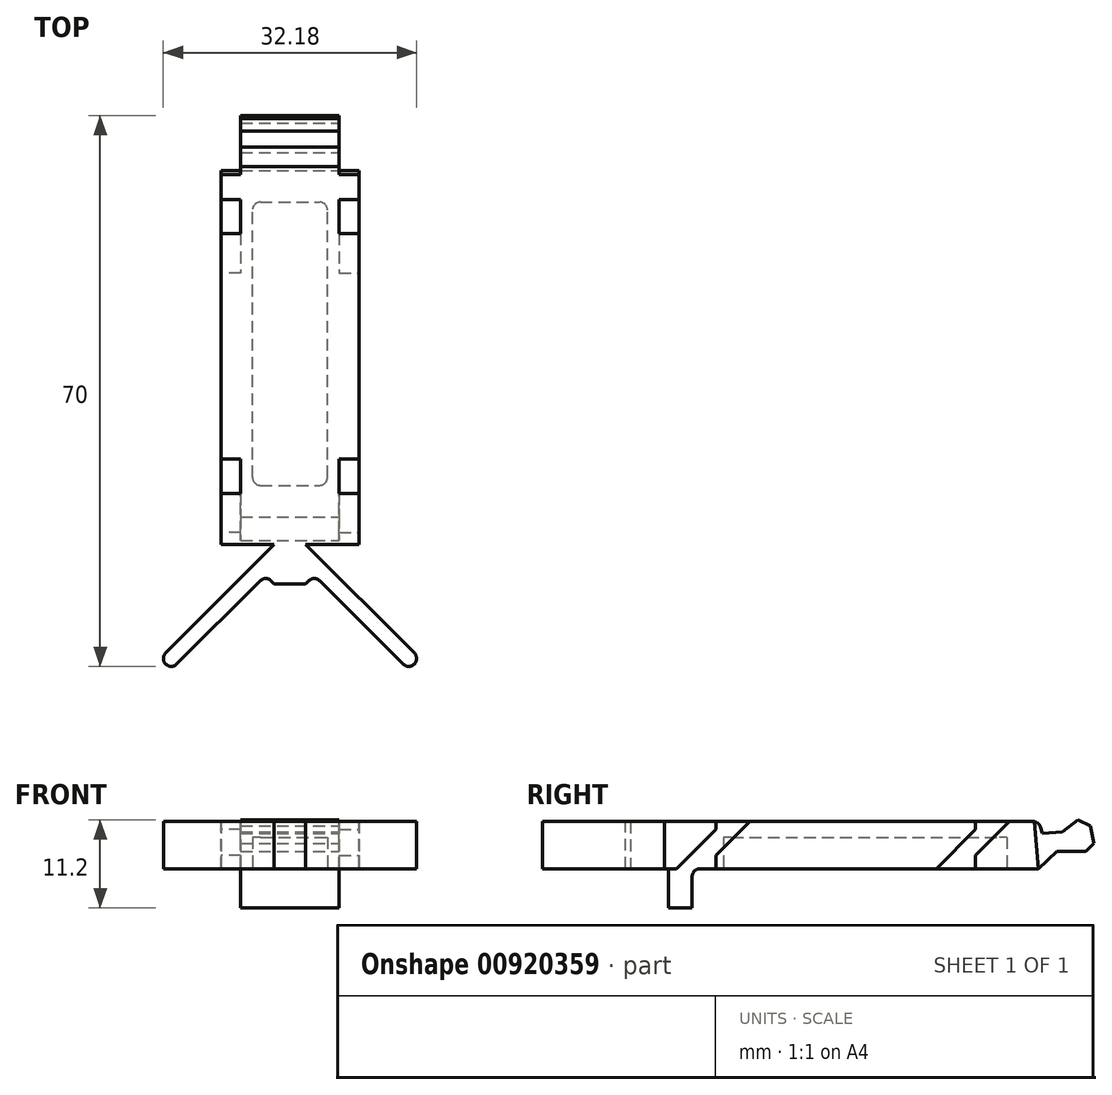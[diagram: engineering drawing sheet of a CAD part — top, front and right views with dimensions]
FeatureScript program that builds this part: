
annotation { "Feature Type Name" : "Feature", "Feature Type Description" : "" }
export const myFeature = defineFeature(function(context is Context, id is Id, definition is map)
    precondition{}
    {
        {
            var Q0;
            Q0=qCreatedBy(makeId("Right.planeOp"),FACE);
            var sketch = newSketch(context, id + "F0", { "sketchPlane" : qUnion([Q0])});
            skLineSegment(sketch, "E0.bottom", {"start": v(3, 0) * mm, "end": v(47, 0) * mm});
            skLineSegment(sketch, "E0.top", {"start": v(-0.5, 6) * mm, "end": v(47, 6) * mm});
            skLineSegment(sketch, "E1", {"start": v(47, 6) * mm, "end": v(47.5, 4.5) * mm});
            skLineSegment(sketch, "E2", {"start": v(47.5, 4.5) * mm, "end": v(50, 4.7) * mm});
            skLineSegment(sketch, "E3", {"start": v(52, 6.2) * mm, "end": v(50, 4.7) * mm});
            skLineSegment(sketch, "E4", {"start": v(52, 6.2) * mm, "end": v(53.6, 5.45) * mm});
            skLineSegment(sketch, "E5", {"start": v(53.6, 5.45) * mm, "end": v(54, 3.2) * mm});
            skLineSegment(sketch, "E6", {"start": v(53, 2.2) * mm, "end": v(54, 3.2) * mm});
            skLineSegment(sketch, "E7", {"start": v(53, 2.2) * mm, "end": v(49.3, 2.2) * mm});
            skLineSegment(sketch, "E8", {"start": v(49.3, 2.2) * mm, "end": v(47, 0) * mm});
            skLineSegment(sketch, "E9.top", {"start": v(0, -5) * mm, "end": v(3, -5) * mm});
            skLineSegment(sketch, "E9.left", {"start": v(0, 0) * mm, "end": v(0, -5) * mm});
            skLineSegment(sketch, "E9.right", {"start": v(3, 0) * mm, "end": v(3, -5) * mm});
            skLineSegment(sketch, "E10", {"start": v(0, 0) * mm, "end": v(-0.5, 0) * mm});
            skLineSegment(sketch, "E11", {"start": v(-0.5, 0) * mm, "end": v(-0.5, 6) * mm});
            skSolve(sketch);
        }
        {
            var Q0;
            Q0=makeQuery(id+"F0.imprint","IMPRINT",FACE,{"disambiguationData":[TD([[makeQuery(id+"F0.imprint","IMPRINT",EDGE,{"derivedFrom":sQuery(id+"F0.wireOp",EDGE,"E0.bottom")}),1.0]])]});
            extrude(context, id + "F1", {"entities" : qUnion([Q0]), "oppositeDirection" : true, "depth" : (17.5 / 2) * mm, "offsetDistance" : 25 * mm});
        }
        {
            var Q0;
            Q0=makeQuery(id+"F1.opExtrude","CAP_FACE",FACE,{"disambiguationData":[OSD([sQuery(id+"F0.wireOp",EDGE,"E0.bottom"),sQuery(id+"F0.wireOp",EDGE,"E0.top"),sQuery(id+"F0.wireOp",EDGE,"E0.left"),sQuery(id+"F0.wireOp",EDGE,"E1"),sQuery(id+"F0.wireOp",EDGE,"E2"),sQuery(id+"F0.wireOp",EDGE,"E3"),sQuery(id+"F0.wireOp",EDGE,"E4"),sQuery(id+"F0.wireOp",EDGE,"E5"),sQuery(id+"F0.wireOp",EDGE,"E6"),sQuery(id+"F0.wireOp",EDGE,"E7"),sQuery(id+"F0.wireOp",EDGE,"E8"),sQuery(id+"F0.wireOp",EDGE,"aNBXXahW-gOjJ-Jwd1-zqlN-Yp4owCK9dqC5"),sQuery(id+"F0.wireOp",EDGE,"ZARCzN4I-FOhr-0KRS-TbkK-G5KhNvsp9BvJ"),sQuery(id+"F0.wireOp",EDGE,"wQh7WQI4-VwIE-I1oY-PVTZ-LHgqh0pQGRtQ"),sQuery(id+"F0.wireOp",EDGE,"8AAlagfr-6v5t-paXQ-9fkX-cdchTd0ztlK5"),sQuery(id+"F0.wireOp",EDGE,"tXMYSlsr-eLFK-F21U-8xQ6-JhVVK3gynAGm")])],"isStart":true});
            var sketch = newSketch(context, id + "F2", { "sketchPlane" : qUnion([Q0])});
            skLineSegment(sketch, "E12", {"start": v(10.32, 6) * mm, "end": v(6, 1.68) * mm});
            skLineSegment(sketch, "E13", {"start": v(6, 0) * mm, "end": v(8, 0) * mm});
            skLineSegment(sketch, "E14", {"start": v(8, 0) * mm, "end": v(8, -7.24) * mm});
            skLineSegment(sketch, "E15", {"start": v(8, -7.24) * mm, "end": v(-4.58, -7.24) * mm});
            skLineSegment(sketch, "E16", {"start": v(-4.58, -7.24) * mm, "end": v(-4.58, 0) * mm});
            skLineSegment(sketch, "E17", {"start": v(-4.58, 0) * mm, "end": v(1, 0) * mm});
            skLineSegment(sketch, "E18", {"start": v(1, 0) * mm, "end": v(6, 5) * mm});
            skLineSegment(sketch, "E19", {"start": v(6, 5) * mm, "end": v(6, 6) * mm});
            skLineSegment(sketch, "E20", {"start": v(6, 6) * mm, "end": v(10.32, 6) * mm});
            skLineSegment(sketch, "E21", {"start": v(6, 1.68) * mm, "end": v(6, 0) * mm});
            skLineSegment(sketch, "E22.1.0.0", {"start": v(39, 0) * mm, "end": v(41, 0) * mm});
            skLineSegment(sketch, "E22.1.0.1", {"start": v(39, 5) * mm, "end": v(39, 6) * mm});
            skLineSegment(sketch, "E22.1.0.2", {"start": v(41, -7.24) * mm, "end": v(28.42, -7.24) * mm});
            skLineSegment(sketch, "E22.1.0.3", {"start": v(39, 1.68) * mm, "end": v(39, 0) * mm});
            skLineSegment(sketch, "E22.1.0.4", {"start": v(41, 0) * mm, "end": v(41, -7.24) * mm});
            skLineSegment(sketch, "E22.1.0.5", {"start": v(39, 6) * mm, "end": v(43.32, 6) * mm});
            skLineSegment(sketch, "E22.1.0.6", {"start": v(28.42, 0) * mm, "end": v(34, 0) * mm});
            skLineSegment(sketch, "E22.1.0.7", {"start": v(28.42, -7.24) * mm, "end": v(28.42, 0) * mm});
            skLineSegment(sketch, "E22.1.0.8", {"start": v(34, 0) * mm, "end": v(39, 5) * mm});
            skLineSegment(sketch, "E22.1.0.9", {"start": v(43.32, 6) * mm, "end": v(39, 1.68) * mm});
            skLineSegment(sketch, "E22.2.0.0", {"start": v(72, 0) * mm, "end": v(74, 0) * mm});
            skLineSegment(sketch, "E22.2.0.1", {"start": v(72, 5) * mm, "end": v(72, 6) * mm});
            skLineSegment(sketch, "E22.2.0.2", {"start": v(74, -7.24) * mm, "end": v(61.42, -7.24) * mm});
            skLineSegment(sketch, "E22.2.0.3", {"start": v(72, 1.68) * mm, "end": v(72, 0) * mm});
            skLineSegment(sketch, "E22.2.0.4", {"start": v(74, 0) * mm, "end": v(74, -7.24) * mm});
            skLineSegment(sketch, "E22.2.0.5", {"start": v(72, 6) * mm, "end": v(76.32, 6) * mm});
            skLineSegment(sketch, "E22.2.0.6", {"start": v(61.42, 0) * mm, "end": v(67, 0) * mm});
            skLineSegment(sketch, "E22.2.0.7", {"start": v(61.42, -7.24) * mm, "end": v(61.42, 0) * mm});
            skLineSegment(sketch, "E22.2.0.8", {"start": v(67, 0) * mm, "end": v(72, 5) * mm});
            skLineSegment(sketch, "E22.2.0.9", {"start": v(76.32, 6) * mm, "end": v(72, 1.68) * mm});
            skLineSegment(sketch, "E22.direction1", {"start": v(-4.58, -7.24) * mm, "end": v(28.42, -7.24) * mm, "construction": true});
            skSolve(sketch);
        }
        {
            var Q0;
            Q0 = qSketchRegion(id + "F2", true);
            extrude(context, id + "F3", {"entities" : qUnion([Q0]), "operationType" : NewBodyOperationType.REMOVE, "oppositeDirection" : true, "depth" : 2.5 * mm, "offsetDistance" : 25 * mm});
        }
        {
            var Q0;
            Q0=makeQuery(id+"F1.opExtrude","SWEPT_EDGE",EDGE,{"disambiguationData":[OSD([sQuery(id+"F0.wireOp",EDGE,"E0.top"),sQuery(id+"F0.wireOp",EDGE,"E1")])]});
            fillet(context, id + "F4", {"entities" : qUnion([Q0]), "radius" : 1 * mm, "tangentPropagation" : true, "allowEdgeOverflow" : false});
        }
        {
            var Q0;
            Q0=makeQuery(id+"F1.opExtrude","SWEPT_FACE",FACE,{"disambiguationData":[OSD([sQuery(id+"F0.wireOp",EDGE,"E0.top")])]});
            var sketch = newSketch(context, id + "F5", { "sketchPlane" : qUnion([Q0])});
            skLineSegment(sketch, "E23", {"start": v(-8.75, -0.5) * mm, "end": v(-8.75, -5.5) * mm});
            skLineSegment(sketch, "E24", {"start": v(-8.75, -5.5) * mm, "end": v(-6.75, -5.5) * mm});
            skLineSegment(sketch, "E25", {"start": v(-6.75, -5.5) * mm, "end": v(-5.66, -4.41) * mm});
            skLineSegment(sketch, "E26", {"start": v(-5.66, -4.41) * mm, "end": v(5.63, -15.7) * mm});
            skLineSegment(sketch, "E27", {"start": v(7.04, -14.3) * mm, "end": v(-6.75, -0.5) * mm});
            skLineSegment(sketch, "E28", {"start": v(-6.75, -0.5) * mm, "end": v(-8.75, -0.5) * mm});
            skArc(sketch, "E29", {"start": v(5.63, -15.7) * mm, "mid": v(7.04, -15.7) * mm, "end": v(7.04, -14.3) * mm});
            skSolve(sketch);
        }
        {
            var Q0;
            Q0 = qSketchRegion(id + "F5", true);
            var Q1;
            Q1=makeQuery(id+"F3.boolean.opBoolean","MERGE",FACE,{"derivedFrom":[makeQuery(id+"F1.opExtrude","SWEPT_FACE",FACE,{"disambiguationData":[OSD([sQuery(id+"F0.wireOp",EDGE,"E10")])]})],"fromTools":[makeQuery(id+"F3.opExtrude","SWEPT_FACE",FACE,{"disambiguationData":[OSD([sQuery(id+"F2.wireOp",EDGE,"E17")])]})]});
            extrude(context, id + "F6", {"entities" : qUnion([Q0]), "operationType" : NewBodyOperationType.ADD, "endBound" : BoundingType.UP_TO_SURFACE, "oppositeDirection" : true, "depth" : 25 * mm, "endBoundEntityFace" : qUnion([Q1]), "offsetDistance" : 25 * mm});
        }
        {
            var Q0;
            {var subQ0=sQuery(id+"F0.wireOp",EDGE,"E7");var subQ1=sQuery(id+"F0.wireOp",EDGE,"E6");var subQ2=sQuery(id+"F0.wireOp",EDGE,"E5");var subQ3=sQuery(id+"F0.wireOp",EDGE,"E4");var subQ4=sQuery(id+"F0.wireOp",EDGE,"E3");var subQ5=sQuery(id+"F0.wireOp",EDGE,"E8");var subQ6=sQuery(id+"F0.wireOp",EDGE,"E0.bottom");var subQ7=sQuery(id+"F0.wireOp",EDGE,"E2");var subQ8=sQuery(id+"F0.wireOp",EDGE,"E0.top");var subQ9=sQuery(id+"F0.wireOp",EDGE,"E1");Q0=makeQuery(id+"F3.boolean.opBoolean","SPLIT",FACE,{"disambiguationData":[TD([makeQuery(id+"F1.opExtrude","SWEPT_FACE",FACE,{"disambiguationData":[OSD([subQ9])]})])],"derivedFrom":makeQuery(id+"F1.opExtrude","CAP_FACE",FACE,{"disambiguationData":[OSD([subQ6,subQ8,subQ9,subQ7,subQ4,subQ3,subQ2,subQ1,subQ0,subQ5,sQuery(id+"F0.wireOp",EDGE,"E9.top"),sQuery(id+"F0.wireOp",EDGE,"E9.left"),sQuery(id+"F0.wireOp",EDGE,"E9.right"),sQuery(id+"F0.wireOp",EDGE,"E10"),sQuery(id+"F0.wireOp",EDGE,"E11")])],"isStart":true})});}
            var sketch = newSketch(context, id + "F7", { "sketchPlane" : qUnion([Q0])});
            skLineSegment(sketch, "E30", {"start": v(46.5, 6) * mm, "end": v(47, 0) * mm});
            skLineSegment(sketch, "E31", {"start": v(47, 0) * mm, "end": v(57.13, 0) * mm});
            skLineSegment(sketch, "E32", {"start": v(57.13, 0) * mm, "end": v(57.13, 7.92) * mm});
            skLineSegment(sketch, "E33", {"start": v(57.13, 7.92) * mm, "end": v(46.5, 7.92) * mm});
            skLineSegment(sketch, "E34", {"start": v(46.5, 7.92) * mm, "end": v(46.5, 6) * mm});
            skSolve(sketch);
        }
        {
            var Q0;
            Q0 = qSketchRegion(id + "F7", true);
            extrude(context, id + "F8", {"entities" : qUnion([Q0]), "operationType" : NewBodyOperationType.REMOVE, "oppositeDirection" : true, "depth" : 2.5 * mm, "offsetDistance" : 25 * mm});
        }
        {
            var Q0;
            Q0=makeQuery(id+"F6.opExtrude","SWEPT_EDGE",EDGE,{"disambiguationData":[OSD([sQuery(id+"F0.wireOp",EDGE,"E0.top"),sQuery(id+"F0.wireOp",EDGE,"E11"),sQuery(id+"F5.wireOp",EDGE,"E27"),sQuery(id+"F5.wireOp",EDGE,"E28")])]});
            var Q1;
            Q1=makeQuery(id+"F6.opExtrude","SWEPT_EDGE",EDGE,{"disambiguationData":[OSD([sQuery(id+"F5.wireOp",EDGE,"E25"),sQuery(id+"F5.wireOp",EDGE,"E26")])]});
            var Q2;
            Q2=makeQuery(id+"F1.opExtrude","SWEPT_EDGE",EDGE,{"disambiguationData":[OSD([sQuery(id+"F0.wireOp",EDGE,"E0.bottom"),sQuery(id+"F0.wireOp",EDGE,"E9.right")])]});
            fillet(context, id + "F9", {"entities" : qUnion([Q0, Q1, Q2]), "radius" : 1 * mm, "tangentPropagation" : true, "allowEdgeOverflow" : false});
        }
        {
            var Q0;
            Q0=makeQuery(id+"F1.opExtrude","SWEPT_BODY",BODY,{"disambiguationData":[OSD([sQuery(id+"F0.wireOp",EDGE,"E0.bottom"),sQuery(id+"F0.wireOp",EDGE,"E0.top"),sQuery(id+"F0.wireOp",EDGE,"E0.left"),sQuery(id+"F0.wireOp",EDGE,"E1"),sQuery(id+"F0.wireOp",EDGE,"E2"),sQuery(id+"F0.wireOp",EDGE,"E3"),sQuery(id+"F0.wireOp",EDGE,"E4"),sQuery(id+"F0.wireOp",EDGE,"E5"),sQuery(id+"F0.wireOp",EDGE,"E6"),sQuery(id+"F0.wireOp",EDGE,"E7"),sQuery(id+"F0.wireOp",EDGE,"E8"),sQuery(id+"F0.wireOp",EDGE,"aNBXXahW-gOjJ-Jwd1-zqlN-Yp4owCK9dqC5"),sQuery(id+"F0.wireOp",EDGE,"ZARCzN4I-FOhr-0KRS-TbkK-G5KhNvsp9BvJ"),sQuery(id+"F0.wireOp",EDGE,"wQh7WQI4-VwIE-I1oY-PVTZ-LHgqh0pQGRtQ"),sQuery(id+"F0.wireOp",EDGE,"8AAlagfr-6v5t-paXQ-9fkX-cdchTd0ztlK5"),sQuery(id+"F0.wireOp",EDGE,"tXMYSlsr-eLFK-F21U-8xQ6-JhVVK3gynAGm")])]});
            var Q1;
            Q1=makeQuery(id+"FLCHkwpaVPQr5Rs_1.boolean.opBoolean","MERGE",FACE,{"derivedFrom":[makeQuery(id+"F1.opExtrude","CAP_FACE",FACE,{"disambiguationData":[OSD([sQuery(id+"F0.wireOp",EDGE,"E0.bottom"),sQuery(id+"F0.wireOp",EDGE,"E0.top"),sQuery(id+"F0.wireOp",EDGE,"E0.left"),sQuery(id+"F0.wireOp",EDGE,"E1"),sQuery(id+"F0.wireOp",EDGE,"E2"),sQuery(id+"F0.wireOp",EDGE,"E3"),sQuery(id+"F0.wireOp",EDGE,"E4"),sQuery(id+"F0.wireOp",EDGE,"E5"),sQuery(id+"F0.wireOp",EDGE,"E6"),sQuery(id+"F0.wireOp",EDGE,"E7"),sQuery(id+"F0.wireOp",EDGE,"E8"),sQuery(id+"F0.wireOp",EDGE,"aNBXXahW-gOjJ-Jwd1-zqlN-Yp4owCK9dqC5"),sQuery(id+"F0.wireOp",EDGE,"ZARCzN4I-FOhr-0KRS-TbkK-G5KhNvsp9BvJ"),sQuery(id+"F0.wireOp",EDGE,"wQh7WQI4-VwIE-I1oY-PVTZ-LHgqh0pQGRtQ"),sQuery(id+"F0.wireOp",EDGE,"8AAlagfr-6v5t-paXQ-9fkX-cdchTd0ztlK5"),sQuery(id+"F0.wireOp",EDGE,"tXMYSlsr-eLFK-F21U-8xQ6-JhVVK3gynAGm")])],"isStart":false}),makeQuery(id+"FLCHkwpaVPQr5Rs_1.opExtrude","SWEPT_FACE",FACE,{"disambiguationData":[OSD([sQuery(id+"Fe41J0ZkXof38Or_1.wireOp",EDGE,"FMss3rq8-1YXU-ggMW-ZsP4-kaaEEqU6PGip")])]})]});
            mirror(context, id + "F10", {"operationType" : NewBodyOperationType.ADD, "entities" : qUnion([Q0]), "mirrorPlane" : qUnion([Q1])});
        }
        {
            var Q0;
            {var subQ0=makeQuery(id+"F1.opExtrude","SWEPT_FACE",FACE,{"disambiguationData":[OSD([sQuery(id+"F0.wireOp",EDGE,"E0.bottom")])]});Q0=makeQuery(id+"F10.boolean.opBoolean","MERGE",FACE,{"derivedFrom":[subQ0,makeQuery(id+"F10.opPattern","COPY",FACE,{"derivedFrom":subQ0,"instanceName":"1"})]});}
            var sketch = newSketch(context, id + "F11", { "sketchPlane" : qUnion([Q0])});
            skLineSegment(sketch, "E35.bottom", {"start": v(-13.5, -7) * mm, "end": v(-4, -7) * mm});
            skLineSegment(sketch, "E35.top", {"start": v(-13.5, -43) * mm, "end": v(-4, -43) * mm});
            skLineSegment(sketch, "E35.left", {"start": v(-13.5, -7) * mm, "end": v(-13.5, -43) * mm});
            skLineSegment(sketch, "E35.right", {"start": v(-4, -7) * mm, "end": v(-4, -43) * mm});
            skSolve(sketch);
        }
        {
            var Q0;
            Q0 = qSketchRegion(id + "F11", true);
            extrude(context, id + "F12", {"entities" : qUnion([Q0]), "operationType" : NewBodyOperationType.REMOVE, "oppositeDirection" : true, "depth" : 4 * mm, "offsetDistance" : 25 * mm});
        }
        {
            var Q0;
            Q0=makeQuery(id+"F12.boolean.opBoolean","COPY",EDGE,{"derivedFrom":makeQuery(id+"F12.opExtrude","SWEPT_EDGE",EDGE,{"disambiguationData":[OSD([sQuery(id+"F11.wireOp",EDGE,"E35.bottom"),sQuery(id+"F11.wireOp",EDGE,"E35.left")])]})});
            var Q1;
            Q1=makeQuery(id+"F12.boolean.opBoolean","COPY",EDGE,{"derivedFrom":makeQuery(id+"F12.opExtrude","SWEPT_EDGE",EDGE,{"disambiguationData":[OSD([sQuery(id+"F11.wireOp",EDGE,"E35.bottom"),sQuery(id+"F11.wireOp",EDGE,"E35.right")])]})});
            var Q2;
            Q2=makeQuery(id+"F12.boolean.opBoolean","COPY",EDGE,{"derivedFrom":makeQuery(id+"F12.opExtrude","SWEPT_EDGE",EDGE,{"disambiguationData":[OSD([sQuery(id+"F11.wireOp",EDGE,"E35.top"),sQuery(id+"F11.wireOp",EDGE,"E35.left")])]})});
            var Q3;
            Q3=makeQuery(id+"F12.boolean.opBoolean","COPY",EDGE,{"derivedFrom":makeQuery(id+"F12.opExtrude","SWEPT_EDGE",EDGE,{"disambiguationData":[OSD([sQuery(id+"F11.wireOp",EDGE,"E35.top"),sQuery(id+"F11.wireOp",EDGE,"E35.right")])]})});
            fillet(context, id + "F13", {"entities" : qUnion([Q0, Q1, Q2, Q3]), "radius" : 1 * mm, "tangentPropagation" : true, "allowEdgeOverflow" : false});
        }
    });
